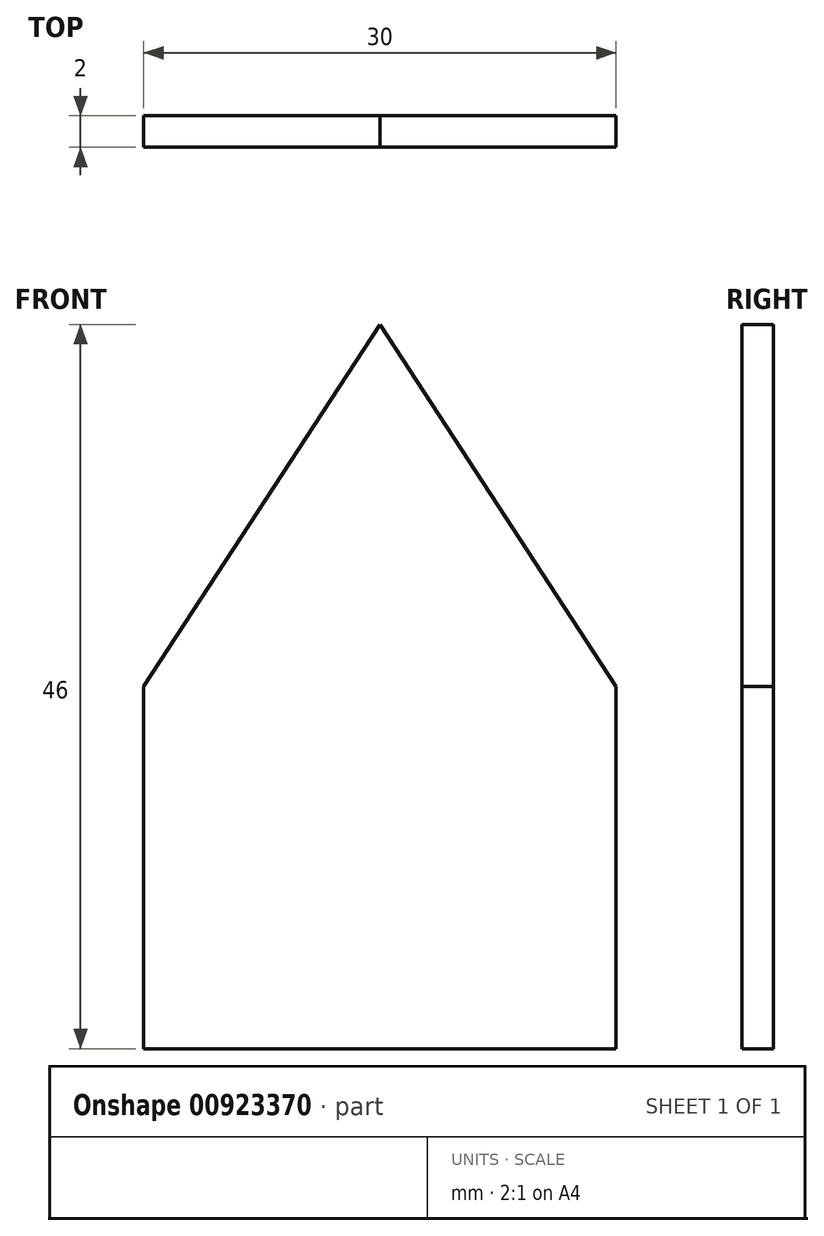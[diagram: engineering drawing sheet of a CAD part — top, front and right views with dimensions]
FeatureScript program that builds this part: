
annotation { "Feature Type Name" : "Feature", "Feature Type Description" : "" }
export const myFeature = defineFeature(function(context is Context, id is Id, definition is map)
    precondition{}
    {
        {
            var Q0;
            Q0=qCreatedBy(makeId("Front.planeOp"),FACE);
            var sketch = newSketch(context, id + "F0", { "sketchPlane" : qUnion([Q0])});
            skLineSegment(sketch, "E0.bottom", {"start": v(15, -11.5) * mm, "end": v(-15, -11.5) * mm});
            skLineSegment(sketch, "E0.left", {"start": v(15, -11.5) * mm, "end": v(15, 11.5) * mm});
            skLineSegment(sketch, "E0.right", {"start": v(-15, -11.5) * mm, "end": v(-15, 11.5) * mm});
            skPoint(sketch, "E0.middle", {"position": v(0, 0) * mm});
            skLineSegment(sketch, "E1", {"start": v(-15, 11.5) * mm, "end": v(0, 34.5) * mm});
            skLineSegment(sketch, "E2", {"start": v(15, 11.5) * mm, "end": v(0, 34.5) * mm});
            skLineSegment(sketch, "E3", {"start": v(0, 34.5) * mm, "end": v(0, -11.5) * mm});
            skLineSegment(sketch, "E4", {"start": v(0, 34.5) * mm, "end": v(0, 44.59) * mm});
            skSolve(sketch);
        }
        {
            var Q0;
            Q0=makeQuery(id+"F0.imprint","IMPRINT",FACE,{"disambiguationData":[TD([[makeQuery(id+"F0.imprint","IMPRINT",EDGE,{"derivedFrom":sQuery(id+"F0.wireOp",EDGE,"E0.bottom")}),-1.0]])]});
            extrude(context, id + "F1", {"entities" : qUnion([Q0]), "depth" : 2 * mm, "offsetDistance" : 25 * mm});
        }
    });
